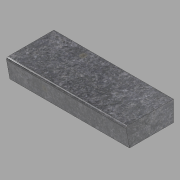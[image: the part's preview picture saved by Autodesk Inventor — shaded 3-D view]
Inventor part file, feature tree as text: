
AUTODESK INVENTOR PART (.ipt)
format: ipt  version: 2022.1 (Build 261234020, 234B)  size: 104,960 bytes
history: native  units: in
note: dims shown in document units (in); Inventor stores cm internally (conversion verified against a paired STEP export)
features: other x3, extrude x1, sketch x1
ambient origin geometry x8: Origin, YZ Plane, XZ Plane, XY Plane, X Axis, Y Axis, Z Axis, Center Point
bodies: Solid1 (feature_tree)
feature tree (5):
  other  "Blocks"
  extrude  "Extrusion1"  Depth=35.375in TaperAngle=0.0deg
  sketch  "Sketch1"  dims[d0=13.0in d1=6.0in d2=13.5in d3=0.5in d4=0.5in d5=35.375in d6=0.0in]
  other  "Profile"
  other  "Profile:1"
